# Revit family: MB-1011
name_source: partatom
category: Plumbing Fixtures
revit_build: Autodesk Revit 2014 (Build: 20130308_1515(x64)
units: mm (PartAtom-declared; Revit-internal decimal feet)

## types (1)
- MB-1011
    Abs Plastic = Plastic
    Air Flow = 291.0 m³/h
    Air Temperature to 4" = 53 °C
    Air Velocity = 16.5 m/s
    Automatic Shut Off = 45.0 s
    Certification = http://www.helvex.com.mx
    Current Consumption = 16 A
    Description = Hand Dryer With Actuator Buttom
    Documentation = http://www.helvex.com.mx
    Drying Time = 35.0 s
    Electrical Protection = Reset Thermostat Thermal Fuse (TCO)
    Features = Push Buttom Operated, 120 VCA Connection Single Phase, 1,20 m Electrical Cable With Plug
    Instructive = http://www.helvex.com.mx
    Manufacturer = HELVEX
    Model = MB-1011
    Noise = 55 dB
    Power Consumption = 1800 W
    Range Of Activation = Self-Adjusting 180 mm Max.
    Total Height = 9"
    Total Length = 11"
    Total Width = 7"
    Type Comments = Electronic Line
    URL = http://www.helvex.com.mx
    Voltage = 120 V
    Voltage 2 = 60

note: source unit labels omitted for Voltage 2 — the stored unit's dimension contradicts the parameter name (converter mislabeling)

## geometry (parser evidence)
native form markers: Sweep x3
no freeform markers — native parametric forms only
